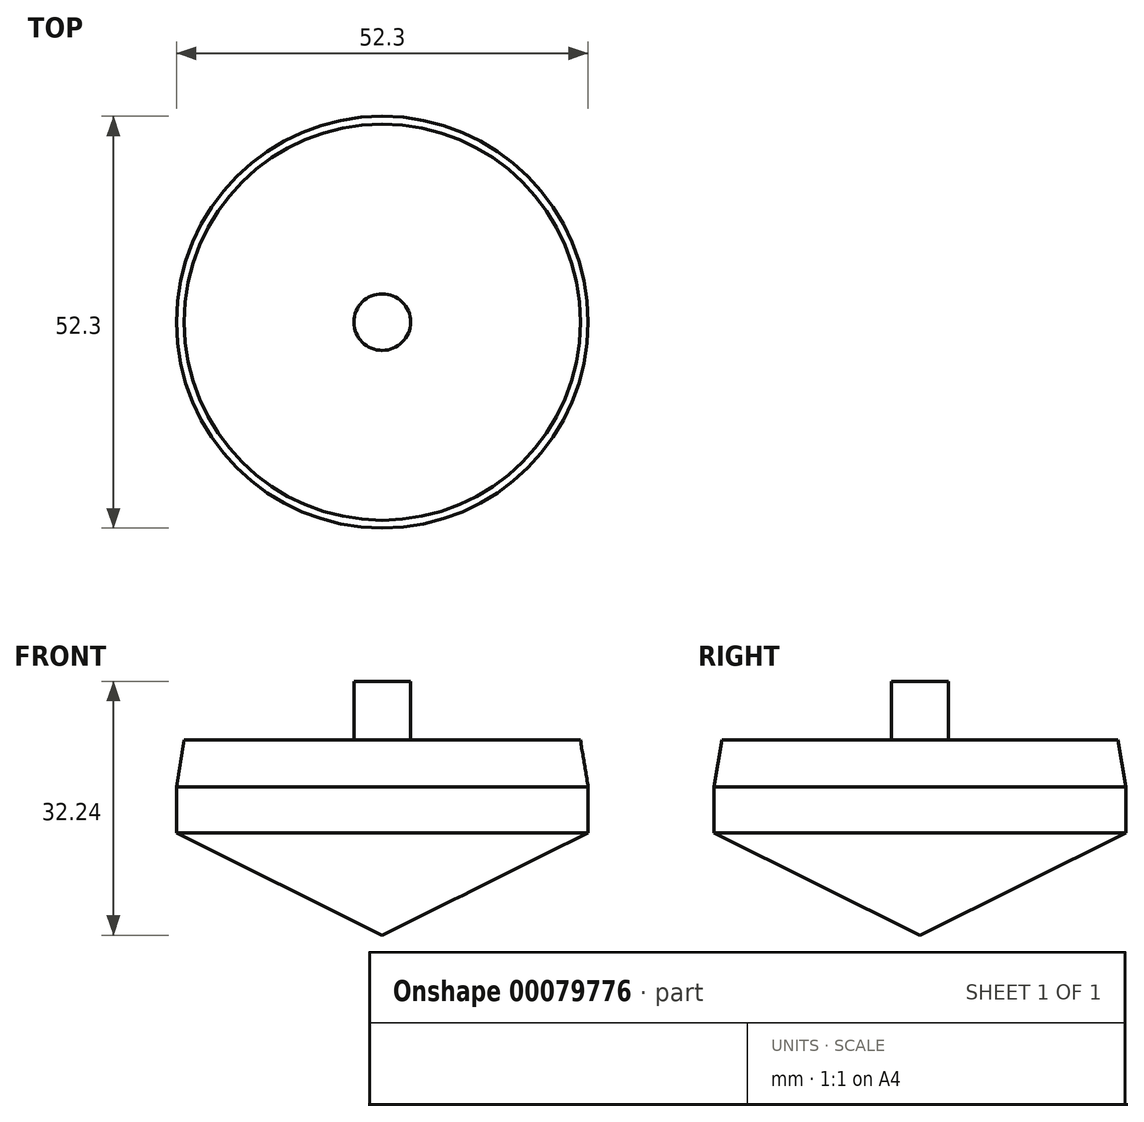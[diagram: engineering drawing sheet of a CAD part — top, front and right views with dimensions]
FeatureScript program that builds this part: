
annotation { "Feature Type Name" : "Feature", "Feature Type Description" : "" }
export const myFeature = defineFeature(function(context is Context, id is Id, definition is map)
    precondition{}
    {
        {
            var Q0;
            Q0=qCreatedBy(makeId("Front.planeOp"),FACE);
            var sketch = newSketch(context, id + "F0", { "sketchPlane" : qUnion([Q0])});
            skPoint(sketch, "E0.startSnap0", {"position": v(13, 13.86) * mm});
            skPoint(sketch, "E1.orphan", {"position": v(17.16, 20.1) * mm});
            skPoint(sketch, "E2.orphan", {"position": v(13, 20.1) * mm});
            skPoint(sketch, "E3.orphan", {"position": v(0, 20.1) * mm});
            skLineSegment(sketch, "E4", {"start": v(0, 0) * mm, "end": v(26.15, 13.02) * mm});
            skPoint(sketch, "E5.end.orphan", {"position": v(8.85, 7.61) * mm});
            skLineSegment(sketch, "E6", {"start": v(26.15, 13.02) * mm, "end": v(26.15, 18.86) * mm});
            skLineSegment(sketch, "E7", {"start": v(0, 18.86) * mm, "end": v(0, 0) * mm});
            skLineSegment(sketch, "E8", {"start": v(0, 18.86) * mm, "end": v(0, 32.24) * mm});
            skLineSegment(sketch, "E9", {"start": v(0, 32.24) * mm, "end": v(3.6, 32.24) * mm});
            skLineSegment(sketch, "E10", {"start": v(3.6, 32.24) * mm, "end": v(3.6, 24.79) * mm});
            skLineSegment(sketch, "E11", {"start": v(3.6, 24.79) * mm, "end": v(25.17, 24.79) * mm});
            skLineSegment(sketch, "E12", {"start": v(25.17, 24.79) * mm, "end": v(26.15, 18.86) * mm});
            skSolve(sketch);
        }
        {
            var Q0;
            Q0 = qSketchRegion(id + "F0", true);
            var Q1;
            Q1=sQuery(id+"F0.wireOp",EDGE,"E7");
            revolve(context, id + "F1", {"entities" : qUnion([Q0]), "axis" : qUnion([Q1]), "revolveType" : RevolveType.FULL});
        }
    });
